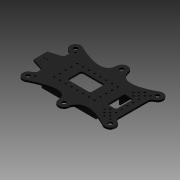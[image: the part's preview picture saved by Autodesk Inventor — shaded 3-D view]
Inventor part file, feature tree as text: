
AUTODESK INVENTOR PART (.ipt)
format: ipt  version: 2012 (Build 160160000, 160)  size: 337,920 bytes
history: native  units: mm
features: extrude x2, sketch x1
ambient origin geometry x8: Origin, YZ Plane, XZ Plane, XY Plane, X Axis, Y Axis, Z Axis, Center Point
feature tree (3):
  sketch  "Sketch1"  dims[d0=10.0mm d13=3.0mm d15=3.0mm d16=3.0mm d18=3.0mm d19=3.0mm d21=6.9mm d22=6.9mm d23=6.9mm d24=6.9mm d25=6.9mm d26=6.9mm d27=12.0mm d28=2.0mm d29=2.0mm d30=5.0mm d39=5.0mm d40=71.014083mm d41=41.0mm d110=3.0mm d118=3.0mm d119=3.0mm d120=3.0mm d121=3.0mm d122=3.0mm d124=7.5mm d126=7.5mm d129=7.5mm d131=7.5mm d133=25.0mm d143=18.0mm d144=18.0mm d152=3.0mm d153=3.0mm d154=3.0mm d155=10.0mm d157=3.0mm d158=3.0mm d159=3.0mm d160=10.0mm d163=12.5mm d164=12.5mm d165=12.5mm d166=12.5mm d167=8.00764mm d168=17.45764mm d169=8.00764mm d170=12.118872mm d175=2.0mm d179=3.0mm d180=0.0mm d181=18.0mm d182=0.0mm d183=10.0mm d185=10.0mm d186=10.0mm d187=10.0mm d205=10.0mm d206=10.0mm d207=10.0mm d208=10.0mm d209=3.0mm d210=3.0mm d211=3.0mm d212=3.0mm d213=18.0mm d215=5.0mm d216=1.0mm d218=18.0mm d224=18.0mm d225=10.0mm d226=10.0mm d227=10.0mm]
  extrude  "Extrusion4"  Depth=3.0mm
  extrude  "Extrusion5"  Depth=18.0mm
